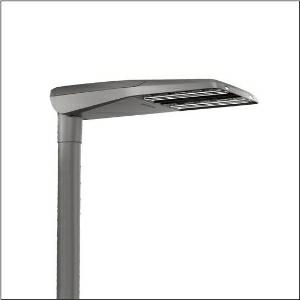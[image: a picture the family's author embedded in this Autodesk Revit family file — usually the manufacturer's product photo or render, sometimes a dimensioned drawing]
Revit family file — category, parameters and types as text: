
# Revit family: streetlight_sl_11_iq_midi___pc-l_5xc3e41e08me_b69f
name_source: partatom
category: Lighting Fixtures
units: mm (PartAtom-declared; Revit-internal decimal feet)

## family parameters
Cut with Voids When Loaded = No
Host = Face
Light Source = No
Part Type = Normal
Room Calculation Point = No
Round Connector Dimension = Use Diameter
Shared = No

## types (1)
- --- (1 x LED, 16220 lm, 124.7 W, 4000K)
    Apparent Load = 125 VA
    CIE Flux Codes = 37 73 96 100 100
    Color Rendering = 70
    Color Temperature = 4000K
    Default Elevation = 1800 mm
    Description = Streetlight SL 11 iQ midi, mast luminaire, primary light control with 3 zone facetted reflector, of plastic, silver coated, highly specular, primary optical cover: cover, of PMMA, transparent, light distribution: PC-L, light emission: direct distribution, primary light characteristic: asymmetric, installation type: post-top, side-entry, LED, High Power LED, rated luminous flux: 16.220lm, luminous efficacy: 130lm/W, light colour: 740, colour temperature: 4000K, control: optimised constant luminous flux control (CLO 2.0), Desk-Remote (wireless, voltage-free reading and setting of iQ features in the workshop via application-optimized NFC function/RFID function), Light-Fading, Smart-Wire, Night-Set, Lumen-Switch, Temp-Guard, Auto-Match, with cable H07RN-F 5x 1.5mm², mains connection: 220..240V, AC, 50/60Hz, connection cable pre-assembled, cable length: 12,5m, start of lifetime: 125W, end of lifetime: 132W, reduction: 61W, luminaire housing, of diecast aluminium, powder-coated, Siteco® metallic grey (DB 702S), length: 780mm, width: 376mm, height: 118mm, spigot size: 60/76mm (post-top) and 42/60/76mm (side-entry), mast flange for spigot size: 42mm: 5XC10008XM4, 60mm: 5XC10008XM2, 76/60mm: 5XC10108XM1, equipment: Power, protection rating (complete): IP66, insulation class (complete): insulation class II (safety insulation), certification: CE, ENEC, VDE, impact resistance: IK09, permissible operating ambient temperature for outdoor applications: -25..+50°C, standard-compliant lighting for roads and squares, packaging unit: 1 piece

Light Distribution: PC-L
    Height = 118 mm
    Lamp = 1 x LED
    Lamp Light Flux = 16220 lm
    Lamp Power = 124.7 W
    Lamp count = 1
    Length = 780 mm
    Luminous efficacy = 130 lm/W
    Manufacturer = Siteco
    ModVariant = No
    Model = 5XC3E41E08ME
    Number of Poles = 1
    OnlyDefault = Yes
    Power Factor = 1
    Product Name = Streetlight SL 11 iQ midi | PC-L
    Product group = mast luminaire | pylon top
    ProductGroupID = 6100
    Protection Class = Protection class II
    Protection Degree = IP 66
    RLX_Detail_Level = 1
    RlxData = <blob elided: 74165 chars, md5=c8fb630a>
    Socket = socket
    Standby Power = 0 W
    System Light Flux = 16220 lm
    System Power = 125 W
    Type Comments = factory setting: luminous flux: 100 % | dim-lin: 254 | 557 mA
    Type Image = l_1005960.jpg
    URL = http://relux.com
    VarID = @adj_118045
    Voltage = 0 V
    Weight = 0.00 kg
    Width = 376 mm

## geometry (parser evidence)
native form markers: Blend x4, Sweep x9
no freeform markers — native parametric forms only
